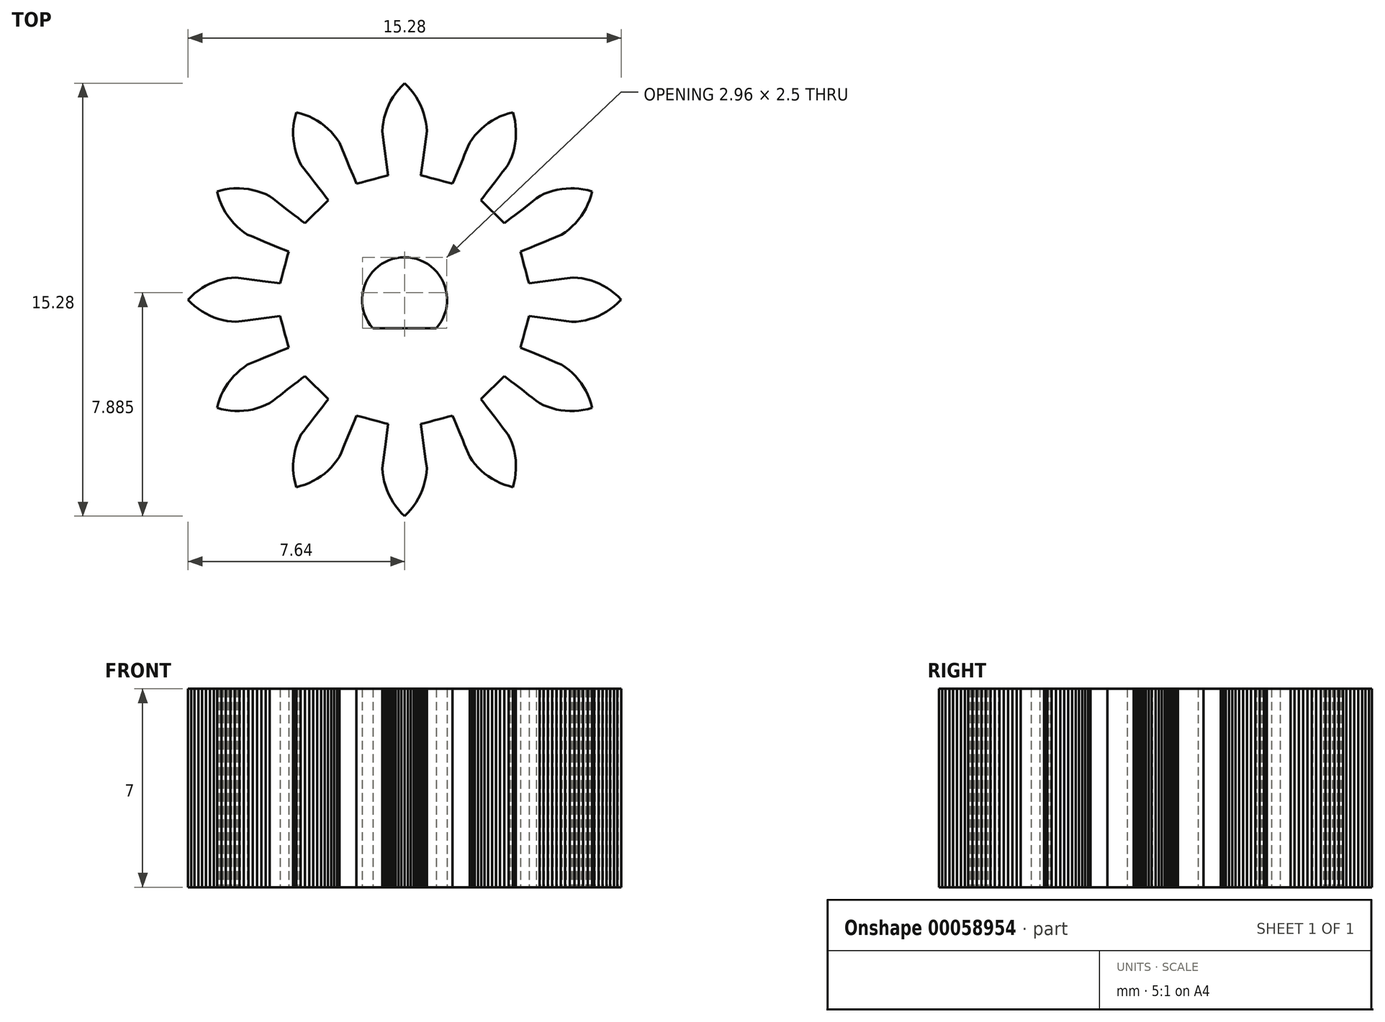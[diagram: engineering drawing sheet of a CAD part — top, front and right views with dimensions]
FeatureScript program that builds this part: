
annotation { "Feature Type Name" : "Feature", "Feature Type Description" : "" }
export const myFeature = defineFeature(function(context is Context, id is Id, definition is map)
    precondition{}
    {
        {
            var Q0;
            Q0=qCreatedBy(makeId("Top.planeOp"),FACE);
            var sketch = newSketch(context, id + "F0", { "sketchPlane" : qUnion([Q0])});
            skLineSegment(sketch, "E0", {"start": v(3.43, -0.58) * mm, "end": v(3.53, -0.6) * mm});
            skLineSegment(sketch, "E1", {"start": v(3.53, -0.6) * mm, "end": v(3.7, -0.61) * mm});
            skLineSegment(sketch, "E2", {"start": v(3.7, -0.61) * mm, "end": v(3.85, -0.63) * mm});
            skLineSegment(sketch, "E3", {"start": v(3.85, -0.63) * mm, "end": v(4, -0.65) * mm});
            skLineSegment(sketch, "E4", {"start": v(4, -0.65) * mm, "end": v(4.16, -0.67) * mm});
            skLineSegment(sketch, "E5", {"start": v(4.16, -0.67) * mm, "end": v(4.31, -0.7) * mm});
            skLineSegment(sketch, "E6", {"start": v(4.31, -0.7) * mm, "end": v(4.47, -0.71) * mm});
            skLineSegment(sketch, "E7", {"start": v(4.47, -0.71) * mm, "end": v(4.62, -0.74) * mm});
            skLineSegment(sketch, "E8", {"start": v(4.62, -0.74) * mm, "end": v(4.78, -0.76) * mm});
            skLineSegment(sketch, "E9", {"start": v(4.78, -0.76) * mm, "end": v(4.94, -0.78) * mm});
            skLineSegment(sketch, "E10", {"start": v(4.94, -0.78) * mm, "end": v(5.1, -0.78) * mm});
            skLineSegment(sketch, "E11", {"start": v(5.1, -0.78) * mm, "end": v(5.26, -0.76) * mm});
            skLineSegment(sketch, "E12", {"start": v(5.26, -0.76) * mm, "end": v(5.43, -0.73) * mm});
            skLineSegment(sketch, "E13", {"start": v(5.43, -0.73) * mm, "end": v(5.59, -0.68) * mm});
            skLineSegment(sketch, "E14", {"start": v(5.59, -0.68) * mm, "end": v(5.74, -0.63) * mm});
            skLineSegment(sketch, "E15", {"start": v(5.74, -0.63) * mm, "end": v(5.89, -0.57) * mm});
            skLineSegment(sketch, "E16", {"start": v(5.89, -0.57) * mm, "end": v(6.03, -0.5) * mm});
            skLineSegment(sketch, "E17", {"start": v(6.03, -0.5) * mm, "end": v(6.17, -0.42) * mm});
            skLineSegment(sketch, "E18", {"start": v(6.17, -0.42) * mm, "end": v(6.3, -0.34) * mm});
            skLineSegment(sketch, "E19", {"start": v(6.3, -0.34) * mm, "end": v(6.43, -0.24) * mm});
            skLineSegment(sketch, "E20", {"start": v(6.43, -0.24) * mm, "end": v(6.55, -0.14) * mm});
            skLineSegment(sketch, "E21", {"start": v(6.55, -0.14) * mm, "end": v(6.66, -0.02) * mm});
            skLineSegment(sketch, "E22", {"start": v(6.66, -0.02) * mm, "end": v(6.68, 0) * mm});
            skLineSegment(sketch, "E23", {"start": v(6.68, 0) * mm, "end": v(6.57, 0.12) * mm});
            skLineSegment(sketch, "E24", {"start": v(6.57, 0.12) * mm, "end": v(6.45, 0.22) * mm});
            skLineSegment(sketch, "E25", {"start": v(6.45, 0.22) * mm, "end": v(6.32, 0.32) * mm});
            skLineSegment(sketch, "E26", {"start": v(6.32, 0.32) * mm, "end": v(6.2, 0.4) * mm});
            skLineSegment(sketch, "E27", {"start": v(6.2, 0.4) * mm, "end": v(6.05, 0.5) * mm});
            skLineSegment(sketch, "E28", {"start": v(6.05, 0.5) * mm, "end": v(5.91, 0.56) * mm});
            skLineSegment(sketch, "E29", {"start": v(5.91, 0.56) * mm, "end": v(5.76, 0.62) * mm});
            skLineSegment(sketch, "E30", {"start": v(5.76, 0.62) * mm, "end": v(5.62, 0.68) * mm});
            skLineSegment(sketch, "E31", {"start": v(5.62, 0.68) * mm, "end": v(5.46, 0.72) * mm});
            skLineSegment(sketch, "E32", {"start": v(5.46, 0.72) * mm, "end": v(5.3, 0.75) * mm});
            skLineSegment(sketch, "E33", {"start": v(5.3, 0.75) * mm, "end": v(5.14, 0.77) * mm});
            skLineSegment(sketch, "E34", {"start": v(5.14, 0.77) * mm, "end": v(4.99, 0.78) * mm});
            skLineSegment(sketch, "E35", {"start": v(4.99, 0.78) * mm, "end": v(4.83, 0.76) * mm});
            skLineSegment(sketch, "E36", {"start": v(4.83, 0.76) * mm, "end": v(4.68, 0.74) * mm});
            skLineSegment(sketch, "E37", {"start": v(4.68, 0.74) * mm, "end": v(4.52, 0.72) * mm});
            skLineSegment(sketch, "E38", {"start": v(4.52, 0.72) * mm, "end": v(4.37, 0.7) * mm});
            skLineSegment(sketch, "E39", {"start": v(4.37, 0.7) * mm, "end": v(4.2, 0.68) * mm});
            skLineSegment(sketch, "E40", {"start": v(4.2, 0.68) * mm, "end": v(4.05, 0.66) * mm});
            skLineSegment(sketch, "E41", {"start": v(4.05, 0.66) * mm, "end": v(3.9, 0.64) * mm});
            skLineSegment(sketch, "E42", {"start": v(3.9, 0.64) * mm, "end": v(3.74, 0.62) * mm});
            skLineSegment(sketch, "E43", {"start": v(3.74, 0.62) * mm, "end": v(3.59, 0.6) * mm});
            skLineSegment(sketch, "E44", {"start": v(3.59, 0.6) * mm, "end": v(3.43, 0.58) * mm});
            skLineSegment(sketch, "E45", {"start": v(3.43, 0.58) * mm, "end": v(3.39, 0.74) * mm});
            skLineSegment(sketch, "E46", {"start": v(3.39, 0.74) * mm, "end": v(3.35, 0.9) * mm});
            skLineSegment(sketch, "E47", {"start": v(3.35, 0.9) * mm, "end": v(3.3, 1.05) * mm});
            skLineSegment(sketch, "E48", {"start": v(3.3, 1.05) * mm, "end": v(3.26, 1.2) * mm});
            skLineSegment(sketch, "E49", {"start": v(3.26, 1.2) * mm, "end": v(3.22, 1.36) * mm});
            skLineSegment(sketch, "E50", {"start": v(3.22, 1.36) * mm, "end": v(3.18, 1.52) * mm});
            skLineSegment(sketch, "E51", {"start": v(3.18, 1.52) * mm, "end": v(3.14, 1.68) * mm});
            skLineSegment(sketch, "E52", {"start": v(3.14, 1.68) * mm, "end": v(3.13, 1.7) * mm});
            skLineSegment(sketch, "E53", {"start": v(3.13, 1.7) * mm, "end": v(3.28, 1.76) * mm});
            skLineSegment(sketch, "E54", {"start": v(3.28, 1.76) * mm, "end": v(3.42, 1.82) * mm});
            skLineSegment(sketch, "E55", {"start": v(3.42, 1.82) * mm, "end": v(3.57, 1.88) * mm});
            skLineSegment(sketch, "E56", {"start": v(3.57, 1.88) * mm, "end": v(3.71, 1.94) * mm});
            skLineSegment(sketch, "E57", {"start": v(3.71, 1.94) * mm, "end": v(3.86, 2) * mm});
            skLineSegment(sketch, "E58", {"start": v(3.86, 2) * mm, "end": v(4, 2.06) * mm});
            skLineSegment(sketch, "E59", {"start": v(4, 2.06) * mm, "end": v(4.15, 2.12) * mm});
            skLineSegment(sketch, "E60", {"start": v(4.15, 2.12) * mm, "end": v(4.3, 2.18) * mm});
            skLineSegment(sketch, "E61", {"start": v(4.3, 2.18) * mm, "end": v(4.44, 2.24) * mm});
            skLineSegment(sketch, "E62", {"start": v(4.44, 2.24) * mm, "end": v(4.58, 2.3) * mm});
            skLineSegment(sketch, "E63", {"start": v(4.58, 2.3) * mm, "end": v(4.72, 2.39) * mm});
            skLineSegment(sketch, "E64", {"start": v(4.72, 2.39) * mm, "end": v(4.84, 2.48) * mm});
            skLineSegment(sketch, "E65", {"start": v(4.84, 2.48) * mm, "end": v(4.96, 2.6) * mm});
            skLineSegment(sketch, "E66", {"start": v(4.96, 2.6) * mm, "end": v(5.07, 2.7) * mm});
            skLineSegment(sketch, "E67", {"start": v(5.07, 2.7) * mm, "end": v(5.18, 2.83) * mm});
            skLineSegment(sketch, "E68", {"start": v(5.18, 2.83) * mm, "end": v(5.27, 2.95) * mm});
            skLineSegment(sketch, "E69", {"start": v(5.27, 2.95) * mm, "end": v(5.36, 3.09) * mm});
            skLineSegment(sketch, "E70", {"start": v(5.36, 3.09) * mm, "end": v(5.44, 3.22) * mm});
            skLineSegment(sketch, "E71", {"start": v(5.44, 3.22) * mm, "end": v(5.5, 3.37) * mm});
            skLineSegment(sketch, "E72", {"start": v(5.5, 3.37) * mm, "end": v(5.57, 3.51) * mm});
            skLineSegment(sketch, "E73", {"start": v(5.57, 3.51) * mm, "end": v(5.62, 3.67) * mm});
            skLineSegment(sketch, "E74", {"start": v(5.62, 3.67) * mm, "end": v(5.66, 3.82) * mm});
            skLineSegment(sketch, "E75", {"start": v(5.66, 3.82) * mm, "end": v(5.5, 3.86) * mm});
            skLineSegment(sketch, "E76", {"start": v(5.5, 3.86) * mm, "end": v(5.35, 3.9) * mm});
            skLineSegment(sketch, "E77", {"start": v(5.35, 3.9) * mm, "end": v(5.19, 3.92) * mm});
            skLineSegment(sketch, "E78", {"start": v(5.19, 3.92) * mm, "end": v(5.03, 3.93) * mm});
            skLineSegment(sketch, "E79", {"start": v(5.03, 3.93) * mm, "end": v(4.9, 3.93) * mm});
            skLineSegment(sketch, "E80", {"start": v(4.9, 3.93) * mm, "end": v(4.74, 3.92) * mm});
            skLineSegment(sketch, "E81", {"start": v(4.74, 3.92) * mm, "end": v(4.58, 3.9) * mm});
            skLineSegment(sketch, "E82", {"start": v(4.58, 3.9) * mm, "end": v(4.42, 3.88) * mm});
            skLineSegment(sketch, "E83", {"start": v(4.42, 3.88) * mm, "end": v(4.27, 3.84) * mm});
            skLineSegment(sketch, "E84", {"start": v(4.27, 3.84) * mm, "end": v(4.12, 3.8) * mm});
            skLineSegment(sketch, "E85", {"start": v(4.12, 3.8) * mm, "end": v(3.97, 3.74) * mm});
            skLineSegment(sketch, "E86", {"start": v(3.97, 3.74) * mm, "end": v(3.83, 3.67) * mm});
            skLineSegment(sketch, "E87", {"start": v(3.83, 3.67) * mm, "end": v(3.7, 3.57) * mm});
            skLineSegment(sketch, "E88", {"start": v(3.7, 3.57) * mm, "end": v(3.56, 3.47) * mm});
            skLineSegment(sketch, "E89", {"start": v(3.56, 3.47) * mm, "end": v(3.43, 3.37) * mm});
            skLineSegment(sketch, "E90", {"start": v(3.43, 3.37) * mm, "end": v(3.3, 3.27) * mm});
            skLineSegment(sketch, "E91", {"start": v(3.3, 3.27) * mm, "end": v(3.18, 3.17) * mm});
            skLineSegment(sketch, "E92", {"start": v(3.18, 3.17) * mm, "end": v(3.05, 3.08) * mm});
            skLineSegment(sketch, "E93", {"start": v(3.05, 3.08) * mm, "end": v(2.93, 2.98) * mm});
            skLineSegment(sketch, "E94", {"start": v(2.93, 2.98) * mm, "end": v(2.8, 2.89) * mm});
            skLineSegment(sketch, "E95", {"start": v(2.8, 2.89) * mm, "end": v(2.68, 2.8) * mm});
            skLineSegment(sketch, "E96", {"start": v(2.68, 2.8) * mm, "end": v(2.55, 2.7) * mm});
            skLineSegment(sketch, "E97", {"start": v(2.55, 2.7) * mm, "end": v(2.44, 2.81) * mm});
            skLineSegment(sketch, "E98", {"start": v(2.44, 2.81) * mm, "end": v(2.32, 2.93) * mm});
            skLineSegment(sketch, "E99", {"start": v(2.32, 2.93) * mm, "end": v(2.2, 3.04) * mm});
            skLineSegment(sketch, "E100", {"start": v(2.2, 3.04) * mm, "end": v(2.1, 3.16) * mm});
            skLineSegment(sketch, "E101", {"start": v(2.1, 3.16) * mm, "end": v(1.98, 3.27) * mm});
            skLineSegment(sketch, "E102", {"start": v(1.98, 3.27) * mm, "end": v(1.86, 3.39) * mm});
            skLineSegment(sketch, "E103", {"start": v(1.86, 3.39) * mm, "end": v(1.75, 3.5) * mm});
            skLineSegment(sketch, "E104", {"start": v(1.75, 3.5) * mm, "end": v(1.74, 3.51) * mm});
            skLineSegment(sketch, "E105", {"start": v(1.74, 3.51) * mm, "end": v(1.83, 3.64) * mm});
            skLineSegment(sketch, "E106", {"start": v(1.83, 3.64) * mm, "end": v(1.93, 3.76) * mm});
            skLineSegment(sketch, "E107", {"start": v(1.93, 3.76) * mm, "end": v(2.02, 3.89) * mm});
            skLineSegment(sketch, "E108", {"start": v(2.02, 3.89) * mm, "end": v(2.12, 4.01) * mm});
            skLineSegment(sketch, "E109", {"start": v(2.12, 4.01) * mm, "end": v(2.21, 4.14) * mm});
            skLineSegment(sketch, "E110", {"start": v(2.21, 4.14) * mm, "end": v(2.3, 4.26) * mm});
            skLineSegment(sketch, "E111", {"start": v(2.3, 4.26) * mm, "end": v(2.4, 4.39) * mm});
            skLineSegment(sketch, "E112", {"start": v(2.4, 4.39) * mm, "end": v(2.5, 4.51) * mm});
            skLineSegment(sketch, "E113", {"start": v(2.5, 4.51) * mm, "end": v(2.6, 4.64) * mm});
            skLineSegment(sketch, "E114", {"start": v(2.6, 4.64) * mm, "end": v(2.7, 4.76) * mm});
            skLineSegment(sketch, "E115", {"start": v(2.7, 4.76) * mm, "end": v(2.76, 4.9) * mm});
            skLineSegment(sketch, "E116", {"start": v(2.76, 4.9) * mm, "end": v(2.82, 5.05) * mm});
            skLineSegment(sketch, "E117", {"start": v(2.82, 5.05) * mm, "end": v(2.87, 5.2) * mm});
            skLineSegment(sketch, "E118", {"start": v(2.87, 5.2) * mm, "end": v(2.91, 5.36) * mm});
            skLineSegment(sketch, "E119", {"start": v(2.91, 5.36) * mm, "end": v(2.94, 5.52) * mm});
            skLineSegment(sketch, "E120", {"start": v(2.94, 5.52) * mm, "end": v(2.96, 5.67) * mm});
            skLineSegment(sketch, "E121", {"start": v(2.96, 5.67) * mm, "end": v(2.97, 5.83) * mm});
            skLineSegment(sketch, "E122", {"start": v(2.97, 5.83) * mm, "end": v(2.97, 6) * mm});
            skLineSegment(sketch, "E123", {"start": v(2.97, 6) * mm, "end": v(2.96, 6.15) * mm});
            skLineSegment(sketch, "E124", {"start": v(2.96, 6.15) * mm, "end": v(2.94, 6.3) * mm});
            skLineSegment(sketch, "E125", {"start": v(2.94, 6.3) * mm, "end": v(2.9, 6.47) * mm});
            skLineSegment(sketch, "E126", {"start": v(2.9, 6.47) * mm, "end": v(2.86, 6.62) * mm});
            skLineSegment(sketch, "E127", {"start": v(2.86, 6.62) * mm, "end": v(2.7, 6.58) * mm});
            skLineSegment(sketch, "E128", {"start": v(2.7, 6.58) * mm, "end": v(2.55, 6.53) * mm});
            skLineSegment(sketch, "E129", {"start": v(2.55, 6.53) * mm, "end": v(2.4, 6.47) * mm});
            skLineSegment(sketch, "E130", {"start": v(2.4, 6.47) * mm, "end": v(2.26, 6.4) * mm});
            skLineSegment(sketch, "E131", {"start": v(2.26, 6.4) * mm, "end": v(2.12, 6.32) * mm});
            skLineSegment(sketch, "E132", {"start": v(2.12, 6.32) * mm, "end": v(1.99, 6.23) * mm});
            skLineSegment(sketch, "E133", {"start": v(1.99, 6.23) * mm, "end": v(1.86, 6.13) * mm});
            skLineSegment(sketch, "E134", {"start": v(1.86, 6.13) * mm, "end": v(1.74, 6.03) * mm});
            skLineSegment(sketch, "E135", {"start": v(1.74, 6.03) * mm, "end": v(1.63, 5.92) * mm});
            skLineSegment(sketch, "E136", {"start": v(1.63, 5.92) * mm, "end": v(1.52, 5.8) * mm});
            skLineSegment(sketch, "E137", {"start": v(1.52, 5.8) * mm, "end": v(1.42, 5.67) * mm});
            skLineSegment(sketch, "E138", {"start": v(1.42, 5.67) * mm, "end": v(1.34, 5.54) * mm});
            skLineSegment(sketch, "E139", {"start": v(1.34, 5.54) * mm, "end": v(1.28, 5.4) * mm});
            skLineSegment(sketch, "E140", {"start": v(1.28, 5.4) * mm, "end": v(1.22, 5.25) * mm});
            skLineSegment(sketch, "E141", {"start": v(1.22, 5.25) * mm, "end": v(1.16, 5.1) * mm});
            skLineSegment(sketch, "E142", {"start": v(1.16, 5.1) * mm, "end": v(1.1, 4.96) * mm});
            skLineSegment(sketch, "E143", {"start": v(1.1, 4.96) * mm, "end": v(1.03, 4.82) * mm});
            skLineSegment(sketch, "E144", {"start": v(1.03, 4.82) * mm, "end": v(0.97, 4.67) * mm});
            skLineSegment(sketch, "E145", {"start": v(0.97, 4.67) * mm, "end": v(0.91, 4.53) * mm});
            skLineSegment(sketch, "E146", {"start": v(0.91, 4.53) * mm, "end": v(0.85, 4.38) * mm});
            skLineSegment(sketch, "E147", {"start": v(0.85, 4.38) * mm, "end": v(0.8, 4.24) * mm});
            skLineSegment(sketch, "E148", {"start": v(0.8, 4.24) * mm, "end": v(0.73, 4.1) * mm});
            skLineSegment(sketch, "E149", {"start": v(0.73, 4.1) * mm, "end": v(0.58, 4.13) * mm});
            skLineSegment(sketch, "E150", {"start": v(0.58, 4.13) * mm, "end": v(0.42, 4.18) * mm});
            skLineSegment(sketch, "E151", {"start": v(0.42, 4.18) * mm, "end": v(0.26, 4.22) * mm});
            skLineSegment(sketch, "E152", {"start": v(0.26, 4.22) * mm, "end": v(0.1, 4.26) * mm});
            skLineSegment(sketch, "E153", {"start": v(0.1, 4.26) * mm, "end": v(-0.05, 4.3) * mm});
            skLineSegment(sketch, "E154", {"start": v(-0.05, 4.3) * mm, "end": v(-0.2, 4.34) * mm});
            skLineSegment(sketch, "E155", {"start": v(-0.2, 4.34) * mm, "end": v(-0.36, 4.39) * mm});
            skLineSegment(sketch, "E156", {"start": v(-0.36, 4.39) * mm, "end": v(-0.38, 4.4) * mm});
            skLineSegment(sketch, "E157", {"start": v(-0.38, 4.4) * mm, "end": v(-0.36, 4.55) * mm});
            skLineSegment(sketch, "E158", {"start": v(-0.36, 4.55) * mm, "end": v(-0.34, 4.7) * mm});
            skLineSegment(sketch, "E159", {"start": v(-0.34, 4.7) * mm, "end": v(-0.32, 4.86) * mm});
            skLineSegment(sketch, "E160", {"start": v(-0.32, 4.86) * mm, "end": v(-0.3, 5.01) * mm});
            skLineSegment(sketch, "E161", {"start": v(-0.3, 5.01) * mm, "end": v(-0.28, 5.17) * mm});
            skLineSegment(sketch, "E162", {"start": v(-0.28, 5.17) * mm, "end": v(-0.26, 5.33) * mm});
            skLineSegment(sketch, "E163", {"start": v(-0.26, 5.33) * mm, "end": v(-0.24, 5.48) * mm});
            skLineSegment(sketch, "E164", {"start": v(-0.24, 5.48) * mm, "end": v(-0.22, 5.64) * mm});
            skLineSegment(sketch, "E165", {"start": v(-0.22, 5.64) * mm, "end": v(-0.2, 5.8) * mm});
            skLineSegment(sketch, "E166", {"start": v(-0.2, 5.8) * mm, "end": v(-0.18, 5.95) * mm});
            skLineSegment(sketch, "E167", {"start": v(-0.18, 5.95) * mm, "end": v(-0.2, 6.11) * mm});
            skLineSegment(sketch, "E168", {"start": v(-0.2, 6.11) * mm, "end": v(-0.21, 6.27) * mm});
            skLineSegment(sketch, "E169", {"start": v(-0.21, 6.27) * mm, "end": v(-0.24, 6.42) * mm});
            skLineSegment(sketch, "E170", {"start": v(-0.24, 6.42) * mm, "end": v(-0.28, 6.58) * mm});
            skLineSegment(sketch, "E171", {"start": v(-0.28, 6.58) * mm, "end": v(-0.34, 6.73) * mm});
            skLineSegment(sketch, "E172", {"start": v(-0.34, 6.73) * mm, "end": v(-0.4, 6.87) * mm});
            skLineSegment(sketch, "E173", {"start": v(-0.4, 6.87) * mm, "end": v(-0.47, 7.02) * mm});
            skLineSegment(sketch, "E174", {"start": v(-0.47, 7.02) * mm, "end": v(-0.55, 7.15) * mm});
            skLineSegment(sketch, "E175", {"start": v(-0.55, 7.15) * mm, "end": v(-0.64, 7.29) * mm});
            skLineSegment(sketch, "E176", {"start": v(-0.64, 7.29) * mm, "end": v(-0.74, 7.41) * mm});
            skLineSegment(sketch, "E177", {"start": v(-0.74, 7.41) * mm, "end": v(-0.85, 7.53) * mm});
            skLineSegment(sketch, "E178", {"start": v(-0.85, 7.53) * mm, "end": v(-0.96, 7.64) * mm});
            skLineSegment(sketch, "E179", {"start": v(-0.96, 7.64) * mm, "end": v(-1.08, 7.53) * mm});
            skLineSegment(sketch, "E180", {"start": v(-1.08, 7.53) * mm, "end": v(-1.18, 7.41) * mm});
            skLineSegment(sketch, "E181", {"start": v(-1.18, 7.41) * mm, "end": v(-1.28, 7.28) * mm});
            skLineSegment(sketch, "E182", {"start": v(-1.28, 7.28) * mm, "end": v(-1.37, 7.15) * mm});
            skLineSegment(sketch, "E183", {"start": v(-1.37, 7.15) * mm, "end": v(-1.45, 7.01) * mm});
            skLineSegment(sketch, "E184", {"start": v(-1.45, 7.01) * mm, "end": v(-1.52, 6.87) * mm});
            skLineSegment(sketch, "E185", {"start": v(-1.52, 6.87) * mm, "end": v(-1.58, 6.72) * mm});
            skLineSegment(sketch, "E186", {"start": v(-1.58, 6.72) * mm, "end": v(-1.64, 6.58) * mm});
            skLineSegment(sketch, "E187", {"start": v(-1.64, 6.58) * mm, "end": v(-1.68, 6.42) * mm});
            skLineSegment(sketch, "E188", {"start": v(-1.68, 6.42) * mm, "end": v(-1.71, 6.27) * mm});
            skLineSegment(sketch, "E189", {"start": v(-1.71, 6.27) * mm, "end": v(-1.73, 6.1) * mm});
            skLineSegment(sketch, "E190", {"start": v(-1.73, 6.1) * mm, "end": v(-1.74, 5.95) * mm});
            skLineSegment(sketch, "E191", {"start": v(-1.74, 5.95) * mm, "end": v(-1.72, 5.8) * mm});
            skLineSegment(sketch, "E192", {"start": v(-1.72, 5.8) * mm, "end": v(-1.7, 5.64) * mm});
            skLineSegment(sketch, "E193", {"start": v(-1.7, 5.64) * mm, "end": v(-1.68, 5.48) * mm});
            skLineSegment(sketch, "E194", {"start": v(-1.68, 5.48) * mm, "end": v(-1.66, 5.33) * mm});
            skLineSegment(sketch, "E195", {"start": v(-1.66, 5.33) * mm, "end": v(-1.64, 5.17) * mm});
            skLineSegment(sketch, "E196", {"start": v(-1.64, 5.17) * mm, "end": v(-1.62, 5.01) * mm});
            skLineSegment(sketch, "E197", {"start": v(-1.62, 5.01) * mm, "end": v(-1.6, 4.86) * mm});
            skLineSegment(sketch, "E198", {"start": v(-1.6, 4.86) * mm, "end": v(-1.58, 4.7) * mm});
            skLineSegment(sketch, "E199", {"start": v(-1.58, 4.7) * mm, "end": v(-1.56, 4.55) * mm});
            skLineSegment(sketch, "E200", {"start": v(-1.56, 4.55) * mm, "end": v(-1.54, 4.4) * mm});
            skLineSegment(sketch, "E201", {"start": v(-1.54, 4.4) * mm, "end": v(-1.7, 4.35) * mm});
            skLineSegment(sketch, "E202", {"start": v(-1.7, 4.35) * mm, "end": v(-1.85, 4.3) * mm});
            skLineSegment(sketch, "E203", {"start": v(-1.85, 4.3) * mm, "end": v(-2, 4.27) * mm});
            skLineSegment(sketch, "E204", {"start": v(-2, 4.27) * mm, "end": v(-2.17, 4.22) * mm});
            skLineSegment(sketch, "E205", {"start": v(-2.17, 4.22) * mm, "end": v(-2.32, 4.18) * mm});
            skLineSegment(sketch, "E206", {"start": v(-2.32, 4.18) * mm, "end": v(-2.48, 4.14) * mm});
            skLineSegment(sketch, "E207", {"start": v(-2.48, 4.14) * mm, "end": v(-2.64, 4.1) * mm});
            skLineSegment(sketch, "E208", {"start": v(-2.64, 4.1) * mm, "end": v(-2.66, 4.1) * mm});
            skLineSegment(sketch, "E209", {"start": v(-2.66, 4.1) * mm, "end": v(-2.72, 4.24) * mm});
            skLineSegment(sketch, "E210", {"start": v(-2.72, 4.24) * mm, "end": v(-2.78, 4.38) * mm});
            skLineSegment(sketch, "E211", {"start": v(-2.78, 4.38) * mm, "end": v(-2.84, 4.53) * mm});
            skLineSegment(sketch, "E212", {"start": v(-2.84, 4.53) * mm, "end": v(-2.9, 4.67) * mm});
            skLineSegment(sketch, "E213", {"start": v(-2.9, 4.67) * mm, "end": v(-2.96, 4.82) * mm});
            skLineSegment(sketch, "E214", {"start": v(-2.96, 4.82) * mm, "end": v(-3.02, 4.96) * mm});
            skLineSegment(sketch, "E215", {"start": v(-3.02, 4.96) * mm, "end": v(-3.08, 5.1) * mm});
            skLineSegment(sketch, "E216", {"start": v(-3.08, 5.1) * mm, "end": v(-3.14, 5.25) * mm});
            skLineSegment(sketch, "E217", {"start": v(-3.14, 5.25) * mm, "end": v(-3.2, 5.4) * mm});
            skLineSegment(sketch, "E218", {"start": v(-3.2, 5.4) * mm, "end": v(-3.26, 5.54) * mm});
            skLineSegment(sketch, "E219", {"start": v(-3.26, 5.54) * mm, "end": v(-3.35, 5.68) * mm});
            skLineSegment(sketch, "E220", {"start": v(-3.35, 5.68) * mm, "end": v(-3.44, 5.8) * mm});
            skLineSegment(sketch, "E221", {"start": v(-3.44, 5.8) * mm, "end": v(-3.55, 5.92) * mm});
            skLineSegment(sketch, "E222", {"start": v(-3.55, 5.92) * mm, "end": v(-3.66, 6.03) * mm});
            skLineSegment(sketch, "E223", {"start": v(-3.66, 6.03) * mm, "end": v(-3.79, 6.14) * mm});
            skLineSegment(sketch, "E224", {"start": v(-3.79, 6.14) * mm, "end": v(-3.91, 6.23) * mm});
            skLineSegment(sketch, "E225", {"start": v(-3.91, 6.23) * mm, "end": v(-4.05, 6.32) * mm});
            skLineSegment(sketch, "E226", {"start": v(-4.05, 6.32) * mm, "end": v(-4.18, 6.4) * mm});
            skLineSegment(sketch, "E227", {"start": v(-4.18, 6.4) * mm, "end": v(-4.33, 6.47) * mm});
            skLineSegment(sketch, "E228", {"start": v(-4.33, 6.47) * mm, "end": v(-4.47, 6.53) * mm});
            skLineSegment(sketch, "E229", {"start": v(-4.47, 6.53) * mm, "end": v(-4.63, 6.58) * mm});
            skLineSegment(sketch, "E230", {"start": v(-4.63, 6.58) * mm, "end": v(-4.78, 6.62) * mm});
            skLineSegment(sketch, "E231", {"start": v(-4.78, 6.62) * mm, "end": v(-4.82, 6.46) * mm});
            skLineSegment(sketch, "E232", {"start": v(-4.82, 6.46) * mm, "end": v(-4.86, 6.3) * mm});
            skLineSegment(sketch, "E233", {"start": v(-4.86, 6.3) * mm, "end": v(-4.88, 6.15) * mm});
            skLineSegment(sketch, "E234", {"start": v(-4.88, 6.15) * mm, "end": v(-4.9, 6) * mm});
            skLineSegment(sketch, "E235", {"start": v(-4.9, 6) * mm, "end": v(-4.9, 5.83) * mm});
            skLineSegment(sketch, "E236", {"start": v(-4.9, 5.83) * mm, "end": v(-4.88, 5.67) * mm});
            skLineSegment(sketch, "E237", {"start": v(-4.88, 5.67) * mm, "end": v(-4.86, 5.51) * mm});
            skLineSegment(sketch, "E238", {"start": v(-4.86, 5.51) * mm, "end": v(-4.83, 5.36) * mm});
            skLineSegment(sketch, "E239", {"start": v(-4.83, 5.36) * mm, "end": v(-4.8, 5.2) * mm});
            skLineSegment(sketch, "E240", {"start": v(-4.8, 5.2) * mm, "end": v(-4.74, 5.05) * mm});
            skLineSegment(sketch, "E241", {"start": v(-4.74, 5.05) * mm, "end": v(-4.68, 4.9) * mm});
            skLineSegment(sketch, "E242", {"start": v(-4.68, 4.9) * mm, "end": v(-4.61, 4.76) * mm});
            skLineSegment(sketch, "E243", {"start": v(-4.61, 4.76) * mm, "end": v(-4.52, 4.64) * mm});
            skLineSegment(sketch, "E244", {"start": v(-4.52, 4.64) * mm, "end": v(-4.42, 4.51) * mm});
            skLineSegment(sketch, "E245", {"start": v(-4.42, 4.51) * mm, "end": v(-4.33, 4.39) * mm});
            skLineSegment(sketch, "E246", {"start": v(-4.33, 4.39) * mm, "end": v(-4.23, 4.26) * mm});
            skLineSegment(sketch, "E247", {"start": v(-4.23, 4.26) * mm, "end": v(-4.14, 4.14) * mm});
            skLineSegment(sketch, "E248", {"start": v(-4.14, 4.14) * mm, "end": v(-4.04, 4.01) * mm});
            skLineSegment(sketch, "E249", {"start": v(-4.04, 4.01) * mm, "end": v(-3.94, 3.89) * mm});
            skLineSegment(sketch, "E250", {"start": v(-3.94, 3.89) * mm, "end": v(-3.85, 3.76) * mm});
            skLineSegment(sketch, "E251", {"start": v(-3.85, 3.76) * mm, "end": v(-3.75, 3.64) * mm});
            skLineSegment(sketch, "E252", {"start": v(-3.75, 3.64) * mm, "end": v(-3.66, 3.51) * mm});
            skLineSegment(sketch, "E253", {"start": v(-3.66, 3.51) * mm, "end": v(-3.77, 3.4) * mm});
            skLineSegment(sketch, "E254", {"start": v(-3.77, 3.4) * mm, "end": v(-3.89, 3.28) * mm});
            skLineSegment(sketch, "E255", {"start": v(-3.89, 3.28) * mm, "end": v(-4, 3.17) * mm});
            skLineSegment(sketch, "E256", {"start": v(-4, 3.17) * mm, "end": v(-4.12, 3.05) * mm});
            skLineSegment(sketch, "E257", {"start": v(-4.12, 3.05) * mm, "end": v(-4.23, 2.94) * mm});
            skLineSegment(sketch, "E258", {"start": v(-4.23, 2.94) * mm, "end": v(-4.35, 2.82) * mm});
            skLineSegment(sketch, "E259", {"start": v(-4.35, 2.82) * mm, "end": v(-4.46, 2.7) * mm});
            skLineSegment(sketch, "E260", {"start": v(-4.46, 2.7) * mm, "end": v(-4.47, 2.7) * mm});
            skLineSegment(sketch, "E261", {"start": v(-4.47, 2.7) * mm, "end": v(-4.6, 2.8) * mm});
            skLineSegment(sketch, "E262", {"start": v(-4.6, 2.8) * mm, "end": v(-4.72, 2.89) * mm});
            skLineSegment(sketch, "E263", {"start": v(-4.72, 2.89) * mm, "end": v(-4.85, 2.98) * mm});
            skLineSegment(sketch, "E264", {"start": v(-4.85, 2.98) * mm, "end": v(-4.97, 3.08) * mm});
            skLineSegment(sketch, "E265", {"start": v(-4.97, 3.08) * mm, "end": v(-5.1, 3.17) * mm});
            skLineSegment(sketch, "E266", {"start": v(-5.1, 3.17) * mm, "end": v(-5.22, 3.27) * mm});
            skLineSegment(sketch, "E267", {"start": v(-5.22, 3.27) * mm, "end": v(-5.35, 3.37) * mm});
            skLineSegment(sketch, "E268", {"start": v(-5.35, 3.37) * mm, "end": v(-5.47, 3.46) * mm});
            skLineSegment(sketch, "E269", {"start": v(-5.47, 3.46) * mm, "end": v(-5.6, 3.56) * mm});
            skLineSegment(sketch, "E270", {"start": v(-5.6, 3.56) * mm, "end": v(-5.72, 3.65) * mm});
            skLineSegment(sketch, "E271", {"start": v(-5.72, 3.65) * mm, "end": v(-5.87, 3.72) * mm});
            skLineSegment(sketch, "E272", {"start": v(-5.87, 3.72) * mm, "end": v(-6.01, 3.78) * mm});
            skLineSegment(sketch, "E273", {"start": v(-6.01, 3.78) * mm, "end": v(-6.17, 3.83) * mm});
            skLineSegment(sketch, "E274", {"start": v(-6.17, 3.83) * mm, "end": v(-6.32, 3.87) * mm});
            skLineSegment(sketch, "E275", {"start": v(-6.32, 3.87) * mm, "end": v(-6.48, 3.9) * mm});
            skLineSegment(sketch, "E276", {"start": v(-6.48, 3.9) * mm, "end": v(-6.63, 3.92) * mm});
            skLineSegment(sketch, "E277", {"start": v(-6.63, 3.92) * mm, "end": v(-6.8, 3.93) * mm});
            skLineSegment(sketch, "E278", {"start": v(-6.8, 3.93) * mm, "end": v(-6.82, 3.93) * mm});
            skLineSegment(sketch, "E279", {"start": v(-6.82, 3.93) * mm, "end": v(-6.99, 3.93) * mm});
            skLineSegment(sketch, "E280", {"start": v(-6.99, 3.93) * mm, "end": v(-7.14, 3.91) * mm});
            skLineSegment(sketch, "E281", {"start": v(-7.14, 3.91) * mm, "end": v(-7.3, 3.89) * mm});
            skLineSegment(sketch, "E282", {"start": v(-7.3, 3.89) * mm, "end": v(-7.46, 3.86) * mm});
            skLineSegment(sketch, "E283", {"start": v(-7.46, 3.86) * mm, "end": v(-7.58, 3.82) * mm});
            skLineSegment(sketch, "E284", {"start": v(-7.58, 3.82) * mm, "end": v(-7.54, 3.66) * mm});
            skLineSegment(sketch, "E285", {"start": v(-7.54, 3.66) * mm, "end": v(-7.49, 3.51) * mm});
            skLineSegment(sketch, "E286", {"start": v(-7.49, 3.51) * mm, "end": v(-7.43, 3.36) * mm});
            skLineSegment(sketch, "E287", {"start": v(-7.43, 3.36) * mm, "end": v(-7.36, 3.22) * mm});
            skLineSegment(sketch, "E288", {"start": v(-7.36, 3.22) * mm, "end": v(-7.28, 3.08) * mm});
            skLineSegment(sketch, "E289", {"start": v(-7.28, 3.08) * mm, "end": v(-7.2, 2.95) * mm});
            skLineSegment(sketch, "E290", {"start": v(-7.2, 2.95) * mm, "end": v(-7.1, 2.82) * mm});
            skLineSegment(sketch, "E291", {"start": v(-7.1, 2.82) * mm, "end": v(-7, 2.7) * mm});
            skLineSegment(sketch, "E292", {"start": v(-7, 2.7) * mm, "end": v(-6.88, 2.59) * mm});
            skLineSegment(sketch, "E293", {"start": v(-6.88, 2.59) * mm, "end": v(-6.76, 2.48) * mm});
            skLineSegment(sketch, "E294", {"start": v(-6.76, 2.48) * mm, "end": v(-6.63, 2.38) * mm});
            skLineSegment(sketch, "E295", {"start": v(-6.63, 2.38) * mm, "end": v(-6.5, 2.3) * mm});
            skLineSegment(sketch, "E296", {"start": v(-6.5, 2.3) * mm, "end": v(-6.36, 2.24) * mm});
            skLineSegment(sketch, "E297", {"start": v(-6.36, 2.24) * mm, "end": v(-6.21, 2.18) * mm});
            skLineSegment(sketch, "E298", {"start": v(-6.21, 2.18) * mm, "end": v(-6.07, 2.12) * mm});
            skLineSegment(sketch, "E299", {"start": v(-6.07, 2.12) * mm, "end": v(-5.92, 2.06) * mm});
            skLineSegment(sketch, "E300", {"start": v(-5.92, 2.06) * mm, "end": v(-5.78, 2) * mm});
            skLineSegment(sketch, "E301", {"start": v(-5.78, 2) * mm, "end": v(-5.63, 1.94) * mm});
            skLineSegment(sketch, "E302", {"start": v(-5.63, 1.94) * mm, "end": v(-5.49, 1.88) * mm});
            skLineSegment(sketch, "E303", {"start": v(-5.49, 1.88) * mm, "end": v(-5.34, 1.82) * mm});
            skLineSegment(sketch, "E304", {"start": v(-5.34, 1.82) * mm, "end": v(-5.2, 1.76) * mm});
            skLineSegment(sketch, "E305", {"start": v(-5.2, 1.76) * mm, "end": v(-5.05, 1.7) * mm});
            skLineSegment(sketch, "E306", {"start": v(-5.05, 1.7) * mm, "end": v(-5.1, 1.54) * mm});
            skLineSegment(sketch, "E307", {"start": v(-5.1, 1.54) * mm, "end": v(-5.14, 1.38) * mm});
            skLineSegment(sketch, "E308", {"start": v(-5.14, 1.38) * mm, "end": v(-5.18, 1.22) * mm});
            skLineSegment(sketch, "E309", {"start": v(-5.18, 1.22) * mm, "end": v(-5.22, 1.07) * mm});
            skLineSegment(sketch, "E310", {"start": v(-5.22, 1.07) * mm, "end": v(-5.26, 0.91) * mm});
            skLineSegment(sketch, "E311", {"start": v(-5.26, 0.91) * mm, "end": v(-5.3, 0.75) * mm});
            skLineSegment(sketch, "E312", {"start": v(-5.3, 0.75) * mm, "end": v(-5.35, 0.6) * mm});
            skLineSegment(sketch, "E313", {"start": v(-5.35, 0.6) * mm, "end": v(-5.35, 0.58) * mm});
            skLineSegment(sketch, "E314", {"start": v(-5.35, 0.58) * mm, "end": v(-5.5, 0.6) * mm});
            skLineSegment(sketch, "E315", {"start": v(-5.5, 0.6) * mm, "end": v(-5.66, 0.62) * mm});
            skLineSegment(sketch, "E316", {"start": v(-5.66, 0.62) * mm, "end": v(-5.82, 0.64) * mm});
            skLineSegment(sketch, "E317", {"start": v(-5.82, 0.64) * mm, "end": v(-5.97, 0.66) * mm});
            skLineSegment(sketch, "E318", {"start": v(-5.97, 0.66) * mm, "end": v(-6.13, 0.68) * mm});
            skLineSegment(sketch, "E319", {"start": v(-6.13, 0.68) * mm, "end": v(-6.29, 0.7) * mm});
            skLineSegment(sketch, "E320", {"start": v(-6.29, 0.7) * mm, "end": v(-6.44, 0.72) * mm});
            skLineSegment(sketch, "E321", {"start": v(-6.44, 0.72) * mm, "end": v(-6.6, 0.74) * mm});
            skLineSegment(sketch, "E322", {"start": v(-6.6, 0.74) * mm, "end": v(-6.75, 0.76) * mm});
            skLineSegment(sketch, "E323", {"start": v(-6.75, 0.76) * mm, "end": v(-6.9, 0.78) * mm});
            skLineSegment(sketch, "E324", {"start": v(-6.9, 0.78) * mm, "end": v(-7.07, 0.77) * mm});
            skLineSegment(sketch, "E325", {"start": v(-7.07, 0.77) * mm, "end": v(-7.23, 0.75) * mm});
            skLineSegment(sketch, "E326", {"start": v(-7.23, 0.75) * mm, "end": v(-7.39, 0.72) * mm});
            skLineSegment(sketch, "E327", {"start": v(-7.39, 0.72) * mm, "end": v(-7.54, 0.68) * mm});
            skLineSegment(sketch, "E328", {"start": v(-7.54, 0.68) * mm, "end": v(-7.69, 0.62) * mm});
            skLineSegment(sketch, "E329", {"start": v(-7.69, 0.62) * mm, "end": v(-7.83, 0.56) * mm});
            skLineSegment(sketch, "E330", {"start": v(-7.83, 0.56) * mm, "end": v(-7.98, 0.49) * mm});
            skLineSegment(sketch, "E331", {"start": v(-7.98, 0.49) * mm, "end": v(-8.11, 0.4) * mm});
            skLineSegment(sketch, "E332", {"start": v(-8.11, 0.4) * mm, "end": v(-8.25, 0.32) * mm});
            skLineSegment(sketch, "E333", {"start": v(-8.25, 0.32) * mm, "end": v(-8.37, 0.22) * mm});
            skLineSegment(sketch, "E334", {"start": v(-8.37, 0.22) * mm, "end": v(-8.5, 0.11) * mm});
            skLineSegment(sketch, "E335", {"start": v(-8.5, 0.11) * mm, "end": v(-8.6, 0) * mm});
            skLineSegment(sketch, "E336", {"start": v(-8.6, 0) * mm, "end": v(-8.49, -0.12) * mm});
            skLineSegment(sketch, "E337", {"start": v(-8.49, -0.12) * mm, "end": v(-8.37, -0.22) * mm});
            skLineSegment(sketch, "E338", {"start": v(-8.37, -0.22) * mm, "end": v(-8.24, -0.32) * mm});
            skLineSegment(sketch, "E339", {"start": v(-8.24, -0.32) * mm, "end": v(-8.11, -0.4) * mm});
            skLineSegment(sketch, "E340", {"start": v(-8.11, -0.4) * mm, "end": v(-7.97, -0.5) * mm});
            skLineSegment(sketch, "E341", {"start": v(-7.97, -0.5) * mm, "end": v(-7.83, -0.56) * mm});
            skLineSegment(sketch, "E342", {"start": v(-7.83, -0.56) * mm, "end": v(-7.68, -0.62) * mm});
            skLineSegment(sketch, "E343", {"start": v(-7.68, -0.62) * mm, "end": v(-7.54, -0.68) * mm});
            skLineSegment(sketch, "E344", {"start": v(-7.54, -0.68) * mm, "end": v(-7.38, -0.72) * mm});
            skLineSegment(sketch, "E345", {"start": v(-7.38, -0.72) * mm, "end": v(-7.23, -0.75) * mm});
            skLineSegment(sketch, "E346", {"start": v(-7.23, -0.75) * mm, "end": v(-7.07, -0.77) * mm});
            skLineSegment(sketch, "E347", {"start": v(-7.07, -0.77) * mm, "end": v(-6.9, -0.78) * mm});
            skLineSegment(sketch, "E348", {"start": v(-6.9, -0.78) * mm, "end": v(-6.75, -0.76) * mm});
            skLineSegment(sketch, "E349", {"start": v(-6.75, -0.76) * mm, "end": v(-6.6, -0.74) * mm});
            skLineSegment(sketch, "E350", {"start": v(-6.6, -0.74) * mm, "end": v(-6.44, -0.72) * mm});
            skLineSegment(sketch, "E351", {"start": v(-6.44, -0.72) * mm, "end": v(-6.29, -0.7) * mm});
            skLineSegment(sketch, "E352", {"start": v(-6.29, -0.7) * mm, "end": v(-6.13, -0.68) * mm});
            skLineSegment(sketch, "E353", {"start": v(-6.13, -0.68) * mm, "end": v(-5.97, -0.66) * mm});
            skLineSegment(sketch, "E354", {"start": v(-5.97, -0.66) * mm, "end": v(-5.82, -0.64) * mm});
            skLineSegment(sketch, "E355", {"start": v(-5.82, -0.64) * mm, "end": v(-5.66, -0.62) * mm});
            skLineSegment(sketch, "E356", {"start": v(-5.66, -0.62) * mm, "end": v(-5.5, -0.6) * mm});
            skLineSegment(sketch, "E357", {"start": v(-5.5, -0.6) * mm, "end": v(-5.35, -0.58) * mm});
            skLineSegment(sketch, "E358", {"start": v(-5.35, -0.58) * mm, "end": v(-5.3, -0.74) * mm});
            skLineSegment(sketch, "E359", {"start": v(-5.3, -0.74) * mm, "end": v(-5.27, -0.9) * mm});
            skLineSegment(sketch, "E360", {"start": v(-5.27, -0.9) * mm, "end": v(-5.23, -1.05) * mm});
            skLineSegment(sketch, "E361", {"start": v(-5.23, -1.05) * mm, "end": v(-5.18, -1.2) * mm});
            skLineSegment(sketch, "E362", {"start": v(-5.18, -1.2) * mm, "end": v(-5.14, -1.36) * mm});
            skLineSegment(sketch, "E363", {"start": v(-5.14, -1.36) * mm, "end": v(-5.1, -1.52) * mm});
            skLineSegment(sketch, "E364", {"start": v(-5.1, -1.52) * mm, "end": v(-5.06, -1.68) * mm});
            skLineSegment(sketch, "E365", {"start": v(-5.06, -1.68) * mm, "end": v(-5.05, -1.7) * mm});
            skLineSegment(sketch, "E366", {"start": v(-5.05, -1.7) * mm, "end": v(-5.2, -1.76) * mm});
            skLineSegment(sketch, "E367", {"start": v(-5.2, -1.76) * mm, "end": v(-5.34, -1.82) * mm});
            skLineSegment(sketch, "E368", {"start": v(-5.34, -1.82) * mm, "end": v(-5.49, -1.88) * mm});
            skLineSegment(sketch, "E369", {"start": v(-5.49, -1.88) * mm, "end": v(-5.63, -1.94) * mm});
            skLineSegment(sketch, "E370", {"start": v(-5.63, -1.94) * mm, "end": v(-5.78, -2) * mm});
            skLineSegment(sketch, "E371", {"start": v(-5.78, -2) * mm, "end": v(-5.92, -2.06) * mm});
            skLineSegment(sketch, "E372", {"start": v(-5.92, -2.06) * mm, "end": v(-6.07, -2.12) * mm});
            skLineSegment(sketch, "E373", {"start": v(-6.07, -2.12) * mm, "end": v(-6.21, -2.18) * mm});
            skLineSegment(sketch, "E374", {"start": v(-6.21, -2.18) * mm, "end": v(-6.36, -2.24) * mm});
            skLineSegment(sketch, "E375", {"start": v(-6.36, -2.24) * mm, "end": v(-6.5, -2.3) * mm});
            skLineSegment(sketch, "E376", {"start": v(-6.5, -2.3) * mm, "end": v(-6.64, -2.39) * mm});
            skLineSegment(sketch, "E377", {"start": v(-6.64, -2.39) * mm, "end": v(-6.76, -2.48) * mm});
            skLineSegment(sketch, "E378", {"start": v(-6.76, -2.48) * mm, "end": v(-6.88, -2.6) * mm});
            skLineSegment(sketch, "E379", {"start": v(-6.88, -2.6) * mm, "end": v(-7, -2.7) * mm});
            skLineSegment(sketch, "E380", {"start": v(-7, -2.7) * mm, "end": v(-7.1, -2.83) * mm});
            skLineSegment(sketch, "E381", {"start": v(-7.1, -2.83) * mm, "end": v(-7.2, -2.95) * mm});
            skLineSegment(sketch, "E382", {"start": v(-7.2, -2.95) * mm, "end": v(-7.28, -3.09) * mm});
            skLineSegment(sketch, "E383", {"start": v(-7.28, -3.09) * mm, "end": v(-7.36, -3.22) * mm});
            skLineSegment(sketch, "E384", {"start": v(-7.36, -3.22) * mm, "end": v(-7.43, -3.37) * mm});
            skLineSegment(sketch, "E385", {"start": v(-7.43, -3.37) * mm, "end": v(-7.49, -3.51) * mm});
            skLineSegment(sketch, "E386", {"start": v(-7.49, -3.51) * mm, "end": v(-7.54, -3.67) * mm});
            skLineSegment(sketch, "E387", {"start": v(-7.54, -3.67) * mm, "end": v(-7.58, -3.82) * mm});
            skLineSegment(sketch, "E388", {"start": v(-7.58, -3.82) * mm, "end": v(-7.42, -3.86) * mm});
            skLineSegment(sketch, "E389", {"start": v(-7.42, -3.86) * mm, "end": v(-7.27, -3.9) * mm});
            skLineSegment(sketch, "E390", {"start": v(-7.27, -3.9) * mm, "end": v(-7.1, -3.92) * mm});
            skLineSegment(sketch, "E391", {"start": v(-7.1, -3.92) * mm, "end": v(-6.95, -3.93) * mm});
            skLineSegment(sketch, "E392", {"start": v(-6.95, -3.93) * mm, "end": v(-6.79, -3.93) * mm});
            skLineSegment(sketch, "E393", {"start": v(-6.79, -3.93) * mm, "end": v(-6.63, -3.92) * mm});
            skLineSegment(sketch, "E394", {"start": v(-6.63, -3.92) * mm, "end": v(-6.47, -3.9) * mm});
            skLineSegment(sketch, "E395", {"start": v(-6.47, -3.9) * mm, "end": v(-6.32, -3.87) * mm});
            skLineSegment(sketch, "E396", {"start": v(-6.32, -3.87) * mm, "end": v(-6.16, -3.83) * mm});
            skLineSegment(sketch, "E397", {"start": v(-6.16, -3.83) * mm, "end": v(-6.01, -3.78) * mm});
            skLineSegment(sketch, "E398", {"start": v(-6.01, -3.78) * mm, "end": v(-5.86, -3.72) * mm});
            skLineSegment(sketch, "E399", {"start": v(-5.86, -3.72) * mm, "end": v(-5.72, -3.65) * mm});
            skLineSegment(sketch, "E400", {"start": v(-5.72, -3.65) * mm, "end": v(-5.6, -3.56) * mm});
            skLineSegment(sketch, "E401", {"start": v(-5.6, -3.56) * mm, "end": v(-5.47, -3.46) * mm});
            skLineSegment(sketch, "E402", {"start": v(-5.47, -3.46) * mm, "end": v(-5.35, -3.37) * mm});
            skLineSegment(sketch, "E403", {"start": v(-5.35, -3.37) * mm, "end": v(-5.22, -3.27) * mm});
            skLineSegment(sketch, "E404", {"start": v(-5.22, -3.27) * mm, "end": v(-5.1, -3.17) * mm});
            skLineSegment(sketch, "E405", {"start": v(-5.1, -3.17) * mm, "end": v(-4.97, -3.08) * mm});
            skLineSegment(sketch, "E406", {"start": v(-4.97, -3.08) * mm, "end": v(-4.85, -2.98) * mm});
            skLineSegment(sketch, "E407", {"start": v(-4.85, -2.98) * mm, "end": v(-4.72, -2.89) * mm});
            skLineSegment(sketch, "E408", {"start": v(-4.72, -2.89) * mm, "end": v(-4.6, -2.8) * mm});
            skLineSegment(sketch, "E409", {"start": v(-4.6, -2.8) * mm, "end": v(-4.47, -2.7) * mm});
            skLineSegment(sketch, "E410", {"start": v(-4.47, -2.7) * mm, "end": v(-4.36, -2.81) * mm});
            skLineSegment(sketch, "E411", {"start": v(-4.36, -2.81) * mm, "end": v(-4.24, -2.93) * mm});
            skLineSegment(sketch, "E412", {"start": v(-4.24, -2.93) * mm, "end": v(-4.13, -3.04) * mm});
            skLineSegment(sketch, "E413", {"start": v(-4.13, -3.04) * mm, "end": v(-4.01, -3.16) * mm});
            skLineSegment(sketch, "E414", {"start": v(-4.01, -3.16) * mm, "end": v(-3.9, -3.27) * mm});
            skLineSegment(sketch, "E415", {"start": v(-3.9, -3.27) * mm, "end": v(-3.79, -3.39) * mm});
            skLineSegment(sketch, "E416", {"start": v(-3.79, -3.39) * mm, "end": v(-3.67, -3.5) * mm});
            skLineSegment(sketch, "E417", {"start": v(-3.67, -3.5) * mm, "end": v(-3.66, -3.51) * mm});
            skLineSegment(sketch, "E418", {"start": v(-3.66, -3.51) * mm, "end": v(-3.75, -3.64) * mm});
            skLineSegment(sketch, "E419", {"start": v(-3.75, -3.64) * mm, "end": v(-3.85, -3.76) * mm});
            skLineSegment(sketch, "E420", {"start": v(-3.85, -3.76) * mm, "end": v(-3.94, -3.89) * mm});
            skLineSegment(sketch, "E421", {"start": v(-3.94, -3.89) * mm, "end": v(-4.04, -4.01) * mm});
            skLineSegment(sketch, "E422", {"start": v(-4.04, -4.01) * mm, "end": v(-4.14, -4.14) * mm});
            skLineSegment(sketch, "E423", {"start": v(-4.14, -4.14) * mm, "end": v(-4.23, -4.26) * mm});
            skLineSegment(sketch, "E424", {"start": v(-4.23, -4.26) * mm, "end": v(-4.33, -4.39) * mm});
            skLineSegment(sketch, "E425", {"start": v(-4.33, -4.39) * mm, "end": v(-4.42, -4.51) * mm});
            skLineSegment(sketch, "E426", {"start": v(-4.42, -4.51) * mm, "end": v(-4.52, -4.64) * mm});
            skLineSegment(sketch, "E427", {"start": v(-4.52, -4.64) * mm, "end": v(-4.61, -4.76) * mm});
            skLineSegment(sketch, "E428", {"start": v(-4.61, -4.76) * mm, "end": v(-4.68, -4.9) * mm});
            skLineSegment(sketch, "E429", {"start": v(-4.68, -4.9) * mm, "end": v(-4.74, -5.05) * mm});
            skLineSegment(sketch, "E430", {"start": v(-4.74, -5.05) * mm, "end": v(-4.8, -5.2) * mm});
            skLineSegment(sketch, "E431", {"start": v(-4.8, -5.2) * mm, "end": v(-4.83, -5.36) * mm});
            skLineSegment(sketch, "E432", {"start": v(-4.83, -5.36) * mm, "end": v(-4.86, -5.52) * mm});
            skLineSegment(sketch, "E433", {"start": v(-4.86, -5.52) * mm, "end": v(-4.88, -5.67) * mm});
            skLineSegment(sketch, "E434", {"start": v(-4.88, -5.67) * mm, "end": v(-4.9, -5.83) * mm});
            skLineSegment(sketch, "E435", {"start": v(-4.9, -5.83) * mm, "end": v(-4.9, -6) * mm});
            skLineSegment(sketch, "E436", {"start": v(-4.9, -6) * mm, "end": v(-4.88, -6.15) * mm});
            skLineSegment(sketch, "E437", {"start": v(-4.88, -6.15) * mm, "end": v(-4.86, -6.3) * mm});
            skLineSegment(sketch, "E438", {"start": v(-4.86, -6.3) * mm, "end": v(-4.82, -6.47) * mm});
            skLineSegment(sketch, "E439", {"start": v(-4.82, -6.47) * mm, "end": v(-4.78, -6.62) * mm});
            skLineSegment(sketch, "E440", {"start": v(-4.78, -6.62) * mm, "end": v(-4.62, -6.58) * mm});
            skLineSegment(sketch, "E441", {"start": v(-4.62, -6.58) * mm, "end": v(-4.47, -6.53) * mm});
            skLineSegment(sketch, "E442", {"start": v(-4.47, -6.53) * mm, "end": v(-4.32, -6.47) * mm});
            skLineSegment(sketch, "E443", {"start": v(-4.32, -6.47) * mm, "end": v(-4.18, -6.4) * mm});
            skLineSegment(sketch, "E444", {"start": v(-4.18, -6.4) * mm, "end": v(-4.04, -6.32) * mm});
            skLineSegment(sketch, "E445", {"start": v(-4.04, -6.32) * mm, "end": v(-3.91, -6.23) * mm});
            skLineSegment(sketch, "E446", {"start": v(-3.91, -6.23) * mm, "end": v(-3.78, -6.13) * mm});
            skLineSegment(sketch, "E447", {"start": v(-3.78, -6.13) * mm, "end": v(-3.66, -6.03) * mm});
            skLineSegment(sketch, "E448", {"start": v(-3.66, -6.03) * mm, "end": v(-3.55, -5.92) * mm});
            skLineSegment(sketch, "E449", {"start": v(-3.55, -5.92) * mm, "end": v(-3.44, -5.8) * mm});
            skLineSegment(sketch, "E450", {"start": v(-3.44, -5.8) * mm, "end": v(-3.35, -5.67) * mm});
            skLineSegment(sketch, "E451", {"start": v(-3.35, -5.67) * mm, "end": v(-3.26, -5.54) * mm});
            skLineSegment(sketch, "E452", {"start": v(-3.26, -5.54) * mm, "end": v(-3.2, -5.4) * mm});
            skLineSegment(sketch, "E453", {"start": v(-3.2, -5.4) * mm, "end": v(-3.14, -5.25) * mm});
            skLineSegment(sketch, "E454", {"start": v(-3.14, -5.25) * mm, "end": v(-3.08, -5.1) * mm});
            skLineSegment(sketch, "E455", {"start": v(-3.08, -5.1) * mm, "end": v(-3.02, -4.96) * mm});
            skLineSegment(sketch, "E456", {"start": v(-3.02, -4.96) * mm, "end": v(-2.96, -4.82) * mm});
            skLineSegment(sketch, "E457", {"start": v(-2.96, -4.82) * mm, "end": v(-2.9, -4.67) * mm});
            skLineSegment(sketch, "E458", {"start": v(-2.9, -4.67) * mm, "end": v(-2.84, -4.53) * mm});
            skLineSegment(sketch, "E459", {"start": v(-2.84, -4.53) * mm, "end": v(-2.78, -4.38) * mm});
            skLineSegment(sketch, "E460", {"start": v(-2.78, -4.38) * mm, "end": v(-2.72, -4.24) * mm});
            skLineSegment(sketch, "E461", {"start": v(-2.72, -4.24) * mm, "end": v(-2.66, -4.1) * mm});
            skLineSegment(sketch, "E462", {"start": v(-2.66, -4.1) * mm, "end": v(-2.5, -4.13) * mm});
            skLineSegment(sketch, "E463", {"start": v(-2.5, -4.13) * mm, "end": v(-2.34, -4.18) * mm});
            skLineSegment(sketch, "E464", {"start": v(-2.34, -4.18) * mm, "end": v(-2.18, -4.22) * mm});
            skLineSegment(sketch, "E465", {"start": v(-2.18, -4.22) * mm, "end": v(-2.03, -4.26) * mm});
            skLineSegment(sketch, "E466", {"start": v(-2.03, -4.26) * mm, "end": v(-1.87, -4.3) * mm});
            skLineSegment(sketch, "E467", {"start": v(-1.87, -4.3) * mm, "end": v(-1.71, -4.34) * mm});
            skLineSegment(sketch, "E468", {"start": v(-1.71, -4.34) * mm, "end": v(-1.56, -4.39) * mm});
            skLineSegment(sketch, "E469", {"start": v(-1.56, -4.39) * mm, "end": v(-1.54, -4.4) * mm});
            skLineSegment(sketch, "E470", {"start": v(-1.54, -4.4) * mm, "end": v(-1.56, -4.55) * mm});
            skLineSegment(sketch, "E471", {"start": v(-1.56, -4.55) * mm, "end": v(-1.58, -4.7) * mm});
            skLineSegment(sketch, "E472", {"start": v(-1.58, -4.7) * mm, "end": v(-1.6, -4.86) * mm});
            skLineSegment(sketch, "E473", {"start": v(-1.6, -4.86) * mm, "end": v(-1.62, -5.01) * mm});
            skLineSegment(sketch, "E474", {"start": v(-1.62, -5.01) * mm, "end": v(-1.64, -5.17) * mm});
            skLineSegment(sketch, "E475", {"start": v(-1.64, -5.17) * mm, "end": v(-1.66, -5.33) * mm});
            skLineSegment(sketch, "E476", {"start": v(-1.66, -5.33) * mm, "end": v(-1.68, -5.48) * mm});
            skLineSegment(sketch, "E477", {"start": v(-1.68, -5.48) * mm, "end": v(-1.7, -5.64) * mm});
            skLineSegment(sketch, "E478", {"start": v(-1.7, -5.64) * mm, "end": v(-1.72, -5.8) * mm});
            skLineSegment(sketch, "E479", {"start": v(-1.72, -5.8) * mm, "end": v(-1.74, -5.95) * mm});
            skLineSegment(sketch, "E480", {"start": v(-1.74, -5.95) * mm, "end": v(-1.73, -6.11) * mm});
            skLineSegment(sketch, "E481", {"start": v(-1.73, -6.11) * mm, "end": v(-1.71, -6.27) * mm});
            skLineSegment(sketch, "E482", {"start": v(-1.71, -6.27) * mm, "end": v(-1.68, -6.42) * mm});
            skLineSegment(sketch, "E483", {"start": v(-1.68, -6.42) * mm, "end": v(-1.64, -6.58) * mm});
            skLineSegment(sketch, "E484", {"start": v(-1.64, -6.58) * mm, "end": v(-1.58, -6.73) * mm});
            skLineSegment(sketch, "E485", {"start": v(-1.58, -6.73) * mm, "end": v(-1.52, -6.87) * mm});
            skLineSegment(sketch, "E486", {"start": v(-1.52, -6.87) * mm, "end": v(-1.45, -7.02) * mm});
            skLineSegment(sketch, "E487", {"start": v(-1.45, -7.02) * mm, "end": v(-1.37, -7.15) * mm});
            skLineSegment(sketch, "E488", {"start": v(-1.37, -7.15) * mm, "end": v(-1.28, -7.29) * mm});
            skLineSegment(sketch, "E489", {"start": v(-1.28, -7.29) * mm, "end": v(-1.18, -7.41) * mm});
            skLineSegment(sketch, "E490", {"start": v(-1.18, -7.41) * mm, "end": v(-1.07, -7.53) * mm});
            skLineSegment(sketch, "E491", {"start": v(-1.07, -7.53) * mm, "end": v(-0.96, -7.64) * mm});
            skLineSegment(sketch, "E492", {"start": v(-0.96, -7.64) * mm, "end": v(-0.85, -7.53) * mm});
            skLineSegment(sketch, "E493", {"start": v(-0.85, -7.53) * mm, "end": v(-0.74, -7.41) * mm});
            skLineSegment(sketch, "E494", {"start": v(-0.74, -7.41) * mm, "end": v(-0.64, -7.28) * mm});
            skLineSegment(sketch, "E495", {"start": v(-0.64, -7.28) * mm, "end": v(-0.55, -7.15) * mm});
            skLineSegment(sketch, "E496", {"start": v(-0.55, -7.15) * mm, "end": v(-0.47, -7.01) * mm});
            skLineSegment(sketch, "E497", {"start": v(-0.47, -7.01) * mm, "end": v(-0.4, -6.87) * mm});
            skLineSegment(sketch, "E498", {"start": v(-0.4, -6.87) * mm, "end": v(-0.34, -6.72) * mm});
            skLineSegment(sketch, "E499", {"start": v(-0.34, -6.72) * mm, "end": v(-0.28, -6.58) * mm});
            skLineSegment(sketch, "E500", {"start": v(-0.28, -6.58) * mm, "end": v(-0.24, -6.42) * mm});
            skLineSegment(sketch, "E501", {"start": v(-0.24, -6.42) * mm, "end": v(-0.21, -6.27) * mm});
            skLineSegment(sketch, "E502", {"start": v(-0.21, -6.27) * mm, "end": v(-0.19, -6.1) * mm});
            skLineSegment(sketch, "E503", {"start": v(-0.19, -6.1) * mm, "end": v(-0.18, -5.95) * mm});
            skLineSegment(sketch, "E504", {"start": v(-0.18, -5.95) * mm, "end": v(-0.2, -5.8) * mm});
            skLineSegment(sketch, "E505", {"start": v(-0.2, -5.8) * mm, "end": v(-0.22, -5.64) * mm});
            skLineSegment(sketch, "E506", {"start": v(-0.22, -5.64) * mm, "end": v(-0.24, -5.48) * mm});
            skLineSegment(sketch, "E507", {"start": v(-0.24, -5.48) * mm, "end": v(-0.26, -5.33) * mm});
            skLineSegment(sketch, "E508", {"start": v(-0.26, -5.33) * mm, "end": v(-0.28, -5.17) * mm});
            skLineSegment(sketch, "E509", {"start": v(-0.28, -5.17) * mm, "end": v(-0.3, -5.01) * mm});
            skLineSegment(sketch, "E510", {"start": v(-0.3, -5.01) * mm, "end": v(-0.32, -4.86) * mm});
            skLineSegment(sketch, "E511", {"start": v(-0.32, -4.86) * mm, "end": v(-0.34, -4.7) * mm});
            skLineSegment(sketch, "E512", {"start": v(-0.34, -4.7) * mm, "end": v(-0.36, -4.55) * mm});
            skLineSegment(sketch, "E513", {"start": v(-0.36, -4.55) * mm, "end": v(-0.38, -4.4) * mm});
            skLineSegment(sketch, "E514", {"start": v(-0.38, -4.4) * mm, "end": v(-0.23, -4.35) * mm});
            skLineSegment(sketch, "E515", {"start": v(-0.23, -4.35) * mm, "end": v(-0.07, -4.3) * mm});
            skLineSegment(sketch, "E516", {"start": v(-0.07, -4.3) * mm, "end": v(0.09, -4.27) * mm});
            skLineSegment(sketch, "E517", {"start": v(0.09, -4.27) * mm, "end": v(0.25, -4.22) * mm});
            skLineSegment(sketch, "E518", {"start": v(0.25, -4.22) * mm, "end": v(0.4, -4.18) * mm});
            skLineSegment(sketch, "E519", {"start": v(0.4, -4.18) * mm, "end": v(0.56, -4.14) * mm});
            skLineSegment(sketch, "E520", {"start": v(0.56, -4.14) * mm, "end": v(0.72, -4.1) * mm});
            skLineSegment(sketch, "E521", {"start": v(0.72, -4.1) * mm, "end": v(0.73, -4.1) * mm});
            skLineSegment(sketch, "E522", {"start": v(0.73, -4.1) * mm, "end": v(0.8, -4.24) * mm});
            skLineSegment(sketch, "E523", {"start": v(0.8, -4.24) * mm, "end": v(0.85, -4.38) * mm});
            skLineSegment(sketch, "E524", {"start": v(0.85, -4.38) * mm, "end": v(0.91, -4.53) * mm});
            skLineSegment(sketch, "E525", {"start": v(0.91, -4.53) * mm, "end": v(0.97, -4.67) * mm});
            skLineSegment(sketch, "E526", {"start": v(0.97, -4.67) * mm, "end": v(1.03, -4.82) * mm});
            skLineSegment(sketch, "E527", {"start": v(1.03, -4.82) * mm, "end": v(1.1, -4.96) * mm});
            skLineSegment(sketch, "E528", {"start": v(1.1, -4.96) * mm, "end": v(1.16, -5.1) * mm});
            skLineSegment(sketch, "E529", {"start": v(1.16, -5.1) * mm, "end": v(1.22, -5.25) * mm});
            skLineSegment(sketch, "E530", {"start": v(1.22, -5.25) * mm, "end": v(1.28, -5.4) * mm});
            skLineSegment(sketch, "E531", {"start": v(1.28, -5.4) * mm, "end": v(1.34, -5.54) * mm});
            skLineSegment(sketch, "E532", {"start": v(1.34, -5.54) * mm, "end": v(1.43, -5.68) * mm});
            skLineSegment(sketch, "E533", {"start": v(1.43, -5.68) * mm, "end": v(1.52, -5.8) * mm});
            skLineSegment(sketch, "E534", {"start": v(1.52, -5.8) * mm, "end": v(1.63, -5.92) * mm});
            skLineSegment(sketch, "E535", {"start": v(1.63, -5.92) * mm, "end": v(1.74, -6.03) * mm});
            skLineSegment(sketch, "E536", {"start": v(1.74, -6.03) * mm, "end": v(1.87, -6.14) * mm});
            skLineSegment(sketch, "E537", {"start": v(1.87, -6.14) * mm, "end": v(1.99, -6.23) * mm});
            skLineSegment(sketch, "E538", {"start": v(1.99, -6.23) * mm, "end": v(2.13, -6.32) * mm});
            skLineSegment(sketch, "E539", {"start": v(2.13, -6.32) * mm, "end": v(2.26, -6.4) * mm});
            skLineSegment(sketch, "E540", {"start": v(2.26, -6.4) * mm, "end": v(2.4, -6.47) * mm});
            skLineSegment(sketch, "E541", {"start": v(2.4, -6.47) * mm, "end": v(2.55, -6.53) * mm});
            skLineSegment(sketch, "E542", {"start": v(2.55, -6.53) * mm, "end": v(2.7, -6.58) * mm});
            skLineSegment(sketch, "E543", {"start": v(2.7, -6.58) * mm, "end": v(2.86, -6.62) * mm});
            skLineSegment(sketch, "E544", {"start": v(2.86, -6.62) * mm, "end": v(2.9, -6.46) * mm});
            skLineSegment(sketch, "E545", {"start": v(2.9, -6.46) * mm, "end": v(2.94, -6.3) * mm});
            skLineSegment(sketch, "E546", {"start": v(2.94, -6.3) * mm, "end": v(2.96, -6.15) * mm});
            skLineSegment(sketch, "E547", {"start": v(2.96, -6.15) * mm, "end": v(2.97, -6) * mm});
            skLineSegment(sketch, "E548", {"start": v(2.97, -6) * mm, "end": v(2.97, -5.83) * mm});
            skLineSegment(sketch, "E549", {"start": v(2.97, -5.83) * mm, "end": v(2.96, -5.67) * mm});
            skLineSegment(sketch, "E550", {"start": v(2.96, -5.67) * mm, "end": v(2.94, -5.51) * mm});
            skLineSegment(sketch, "E551", {"start": v(2.94, -5.51) * mm, "end": v(2.91, -5.36) * mm});
            skLineSegment(sketch, "E552", {"start": v(2.91, -5.36) * mm, "end": v(2.87, -5.2) * mm});
            skLineSegment(sketch, "E553", {"start": v(2.87, -5.2) * mm, "end": v(2.82, -5.05) * mm});
            skLineSegment(sketch, "E554", {"start": v(2.82, -5.05) * mm, "end": v(2.76, -4.9) * mm});
            skLineSegment(sketch, "E555", {"start": v(2.76, -4.9) * mm, "end": v(2.7, -4.76) * mm});
            skLineSegment(sketch, "E556", {"start": v(2.7, -4.76) * mm, "end": v(2.6, -4.64) * mm});
            skLineSegment(sketch, "E557", {"start": v(2.6, -4.64) * mm, "end": v(2.5, -4.51) * mm});
            skLineSegment(sketch, "E558", {"start": v(2.5, -4.51) * mm, "end": v(2.4, -4.39) * mm});
            skLineSegment(sketch, "E559", {"start": v(2.4, -4.39) * mm, "end": v(2.3, -4.26) * mm});
            skLineSegment(sketch, "E560", {"start": v(2.3, -4.26) * mm, "end": v(2.21, -4.14) * mm});
            skLineSegment(sketch, "E561", {"start": v(2.21, -4.14) * mm, "end": v(2.12, -4.01) * mm});
            skLineSegment(sketch, "E562", {"start": v(2.12, -4.01) * mm, "end": v(2.02, -3.89) * mm});
            skLineSegment(sketch, "E563", {"start": v(2.02, -3.89) * mm, "end": v(1.93, -3.76) * mm});
            skLineSegment(sketch, "E564", {"start": v(1.93, -3.76) * mm, "end": v(1.83, -3.64) * mm});
            skLineSegment(sketch, "E565", {"start": v(1.83, -3.64) * mm, "end": v(1.74, -3.51) * mm});
            skLineSegment(sketch, "E566", {"start": v(1.74, -3.51) * mm, "end": v(1.85, -3.4) * mm});
            skLineSegment(sketch, "E567", {"start": v(1.85, -3.4) * mm, "end": v(1.97, -3.28) * mm});
            skLineSegment(sketch, "E568", {"start": v(1.97, -3.28) * mm, "end": v(2.08, -3.17) * mm});
            skLineSegment(sketch, "E569", {"start": v(2.08, -3.17) * mm, "end": v(2.2, -3.05) * mm});
            skLineSegment(sketch, "E570", {"start": v(2.2, -3.05) * mm, "end": v(2.31, -2.94) * mm});
            skLineSegment(sketch, "E571", {"start": v(2.31, -2.94) * mm, "end": v(2.43, -2.82) * mm});
            skLineSegment(sketch, "E572", {"start": v(2.43, -2.82) * mm, "end": v(2.54, -2.7) * mm});
            skLineSegment(sketch, "E573", {"start": v(2.54, -2.7) * mm, "end": v(2.55, -2.7) * mm});
            skLineSegment(sketch, "E574", {"start": v(2.55, -2.7) * mm, "end": v(2.68, -2.8) * mm});
            skLineSegment(sketch, "E575", {"start": v(2.68, -2.8) * mm, "end": v(2.8, -2.89) * mm});
            skLineSegment(sketch, "E576", {"start": v(2.8, -2.89) * mm, "end": v(2.93, -2.98) * mm});
            skLineSegment(sketch, "E577", {"start": v(2.93, -2.98) * mm, "end": v(3.05, -3.08) * mm});
            skLineSegment(sketch, "E578", {"start": v(3.05, -3.08) * mm, "end": v(3.18, -3.17) * mm});
            skLineSegment(sketch, "E579", {"start": v(3.18, -3.17) * mm, "end": v(3.3, -3.27) * mm});
            skLineSegment(sketch, "E580", {"start": v(3.3, -3.27) * mm, "end": v(3.43, -3.37) * mm});
            skLineSegment(sketch, "E581", {"start": v(3.43, -3.37) * mm, "end": v(3.55, -3.46) * mm});
            skLineSegment(sketch, "E582", {"start": v(3.55, -3.46) * mm, "end": v(3.67, -3.56) * mm});
            skLineSegment(sketch, "E583", {"start": v(3.67, -3.56) * mm, "end": v(3.8, -3.65) * mm});
            skLineSegment(sketch, "E584", {"start": v(3.8, -3.65) * mm, "end": v(3.95, -3.72) * mm});
            skLineSegment(sketch, "E585", {"start": v(3.95, -3.72) * mm, "end": v(4.1, -3.78) * mm});
            skLineSegment(sketch, "E586", {"start": v(4.1, -3.78) * mm, "end": v(4.25, -3.83) * mm});
            skLineSegment(sketch, "E587", {"start": v(4.25, -3.83) * mm, "end": v(4.4, -3.87) * mm});
            skLineSegment(sketch, "E588", {"start": v(4.4, -3.87) * mm, "end": v(4.56, -3.9) * mm});
            skLineSegment(sketch, "E589", {"start": v(4.56, -3.9) * mm, "end": v(4.71, -3.92) * mm});
            skLineSegment(sketch, "E590", {"start": v(4.71, -3.92) * mm, "end": v(4.87, -3.93) * mm});
            skLineSegment(sketch, "E591", {"start": v(4.87, -3.93) * mm, "end": v(5.03, -3.93) * mm});
            skLineSegment(sketch, "E592", {"start": v(5.03, -3.93) * mm, "end": v(5.2, -3.92) * mm});
            skLineSegment(sketch, "E593", {"start": v(5.2, -3.92) * mm, "end": v(5.35, -3.9) * mm});
            skLineSegment(sketch, "E594", {"start": v(5.35, -3.9) * mm, "end": v(5.5, -3.86) * mm});
            skLineSegment(sketch, "E595", {"start": v(5.5, -3.86) * mm, "end": v(5.66, -3.82) * mm});
            skLineSegment(sketch, "E596", {"start": v(5.66, -3.82) * mm, "end": v(5.61, -3.66) * mm});
            skLineSegment(sketch, "E597", {"start": v(5.61, -3.66) * mm, "end": v(5.57, -3.51) * mm});
            skLineSegment(sketch, "E598", {"start": v(5.57, -3.51) * mm, "end": v(5.5, -3.36) * mm});
            skLineSegment(sketch, "E599", {"start": v(5.5, -3.36) * mm, "end": v(5.44, -3.22) * mm});
            skLineSegment(sketch, "E600", {"start": v(5.44, -3.22) * mm, "end": v(5.36, -3.08) * mm});
            skLineSegment(sketch, "E601", {"start": v(5.36, -3.08) * mm, "end": v(5.27, -2.95) * mm});
            skLineSegment(sketch, "E602", {"start": v(5.27, -2.95) * mm, "end": v(5.17, -2.82) * mm});
            skLineSegment(sketch, "E603", {"start": v(5.17, -2.82) * mm, "end": v(5.07, -2.7) * mm});
            skLineSegment(sketch, "E604", {"start": v(5.07, -2.7) * mm, "end": v(4.96, -2.59) * mm});
            skLineSegment(sketch, "E605", {"start": v(4.96, -2.59) * mm, "end": v(4.84, -2.48) * mm});
            skLineSegment(sketch, "E606", {"start": v(4.84, -2.48) * mm, "end": v(4.71, -2.38) * mm});
            skLineSegment(sketch, "E607", {"start": v(4.71, -2.38) * mm, "end": v(4.58, -2.3) * mm});
            skLineSegment(sketch, "E608", {"start": v(4.58, -2.3) * mm, "end": v(4.44, -2.24) * mm});
            skLineSegment(sketch, "E609", {"start": v(4.44, -2.24) * mm, "end": v(4.3, -2.18) * mm});
            skLineSegment(sketch, "E610", {"start": v(4.3, -2.18) * mm, "end": v(4.15, -2.12) * mm});
            skLineSegment(sketch, "E611", {"start": v(4.15, -2.12) * mm, "end": v(4, -2.06) * mm});
            skLineSegment(sketch, "E612", {"start": v(4, -2.06) * mm, "end": v(3.86, -2) * mm});
            skLineSegment(sketch, "E613", {"start": v(3.86, -2) * mm, "end": v(3.71, -1.94) * mm});
            skLineSegment(sketch, "E614", {"start": v(3.71, -1.94) * mm, "end": v(3.57, -1.88) * mm});
            skLineSegment(sketch, "E615", {"start": v(3.57, -1.88) * mm, "end": v(3.42, -1.82) * mm});
            skLineSegment(sketch, "E616", {"start": v(3.42, -1.82) * mm, "end": v(3.28, -1.76) * mm});
            skLineSegment(sketch, "E617", {"start": v(3.28, -1.76) * mm, "end": v(3.13, -1.7) * mm});
            skLineSegment(sketch, "E618", {"start": v(3.13, -1.7) * mm, "end": v(3.17, -1.54) * mm});
            skLineSegment(sketch, "E619", {"start": v(3.17, -1.54) * mm, "end": v(3.22, -1.38) * mm});
            skLineSegment(sketch, "E620", {"start": v(3.22, -1.38) * mm, "end": v(3.26, -1.22) * mm});
            skLineSegment(sketch, "E621", {"start": v(3.26, -1.22) * mm, "end": v(3.3, -1.07) * mm});
            skLineSegment(sketch, "E622", {"start": v(3.3, -1.07) * mm, "end": v(3.34, -0.91) * mm});
            skLineSegment(sketch, "E623", {"start": v(3.34, -0.91) * mm, "end": v(3.38, -0.75) * mm});
            skLineSegment(sketch, "E624", {"start": v(3.38, -0.75) * mm, "end": v(3.43, -0.6) * mm});
            skLineSegment(sketch, "E625", {"start": v(3.43, -0.6) * mm, "end": v(3.43, -0.58) * mm});
            skPoint(sketch, "E626", {"position": v(-0.96, 0) * mm});
            skCircle(sketch, "E627", {"center": v(-0.96, 0) * mm, "radius": 1.5 * mm});
            skLineSegment(sketch, "E628", {"start": v(-0.96, 1.5) * mm, "end": v(-0.96, -1) * mm, "construction": true});
            skLineSegment(sketch, "E629", {"start": v(-2.08, -1) * mm, "end": v(0.16, -1) * mm});
            skSolve(sketch);
        }
        {
            var Q0;
            Q0=makeQuery(id+"F0.imprint","IMPRINT",FACE,{"disambiguationData":[TD([[makeQuery(id+"F0.imprint","IMPRINT",EDGE,{"derivedFrom":sQuery(id+"F0.wireOp",EDGE,"E0")}),1.0]])]});
            var Q1;
            {var subQ0=sQuery(id+"F0.wireOp",EDGE,"E629");Q1=makeQuery(id+"F0.imprint","IMPRINT",FACE,{"disambiguationData":[TD([[makeQuery(id+"F0.imprint","IMPRINT",EDGE,{"derivedFrom":subQ0}),-1.0]])]});}
            extrude(context, id + "F1", {"entities" : qUnion([Q0, Q1]), "depth" : 7 * mm});
        }
    });
